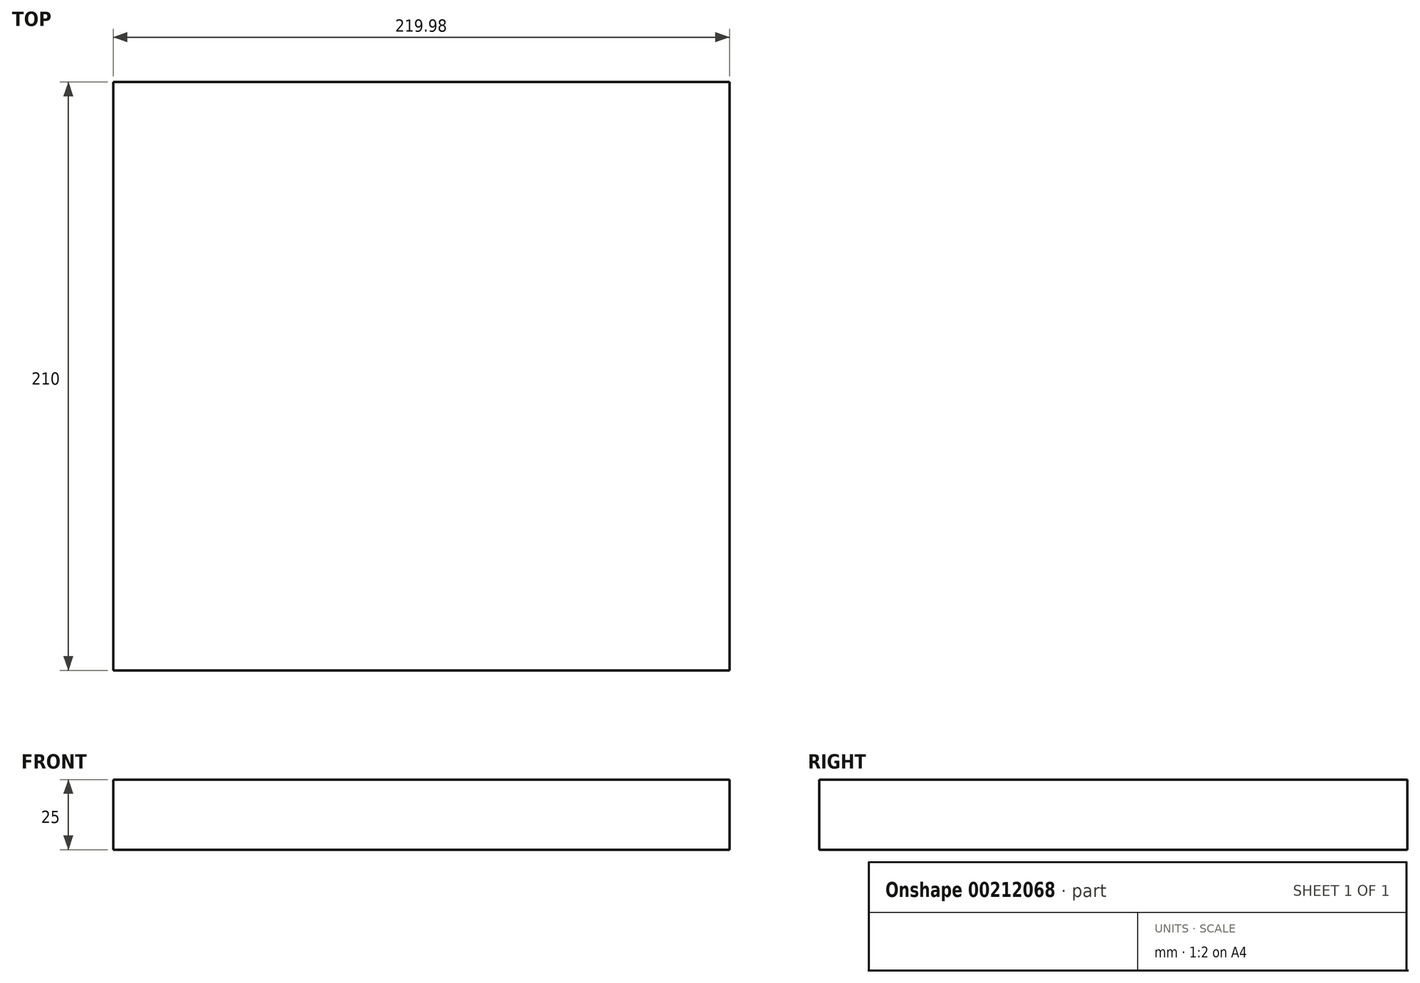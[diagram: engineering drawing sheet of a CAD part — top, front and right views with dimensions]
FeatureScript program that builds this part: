
annotation { "Feature Type Name" : "Feature", "Feature Type Description" : "" }
export const myFeature = defineFeature(function(context is Context, id is Id, definition is map)
    precondition{}
    {
        {
            var Q0;
            Q0=qCreatedBy(makeId("Top.planeOp"),FACE);
            var sketch = newSketch(context, id + "F0", { "sketchPlane" : qUnion([Q0])});
            skLineSegment(sketch, "E0", {"start": v(0, 0) * mm, "end": v(0, 100) * mm, "construction": true});
            skLineSegment(sketch, "E1.bottom", {"start": v(110, 105) * mm, "end": v(-110, 105) * mm});
            skLineSegment(sketch, "E1.top", {"start": v(110, -105) * mm, "end": v(-110, -105) * mm});
            skLineSegment(sketch, "E1.left", {"start": v(110, 105) * mm, "end": v(110, -105) * mm});
            skLineSegment(sketch, "E1.right", {"start": v(-110, 105) * mm, "end": v(-110, -105) * mm});
            skPoint(sketch, "E1.middle", {"position": v(0, 0) * mm});
            skSolve(sketch);
        }
        {
            var Q0;
            Q0 = qSketchRegion(id + "F0", true);
            extrude(context, id + "F1", {"entities" : qUnion([Q0]), "depth" : 25 * mm});
        }
        {
            var Q0;
            Q0=makeQuery(id+"F1.opExtrude","CAP_FACE",FACE,{"disambiguationData":[OSD([sQuery(id+"F0.wireOp",EDGE,"E1.bottom"),sQuery(id+"F0.wireOp",EDGE,"E1.top"),sQuery(id+"F0.wireOp",EDGE,"E1.left"),sQuery(id+"F0.wireOp",EDGE,"E1.right")])],"isStart":false});
            var sketch = newSketch(context, id + "F2", { "sketchPlane" : qUnion([Q0])});
            skLineSegment(sketch, "E2.bottom", {"start": v(84.38, 90) * mm, "end": v(-84.38, 90) * mm});
            skLineSegment(sketch, "E2.top", {"start": v(84.38, -90) * mm, "end": v(-84.38, -90) * mm});
            skLineSegment(sketch, "E2.left", {"start": v(84.38, 90) * mm, "end": v(84.38, -90) * mm});
            skLineSegment(sketch, "E2.right", {"start": v(-84.38, 90) * mm, "end": v(-84.38, -90) * mm});
            skPoint(sketch, "E2.middle", {"position": v(0, 0) * mm});
            skSolve(sketch);
        }
        {
            var Q0;
            Q0=makeQuery(id+"F2.imprint","IMPRINT",FACE,{"disambiguationData":[TD([[makeQuery(id+"F2.imprint","IMPRINT",EDGE,{"derivedFrom":sQuery(id+"F2.wireOp",EDGE,"E2.bottom")}),1.0]])]});
            extrude(context, id + "F3", {"entities" : qUnion([Q0]), "operationType" : NewBodyOperationType.REMOVE, "depth" : 8 * mm});
        }
    });
